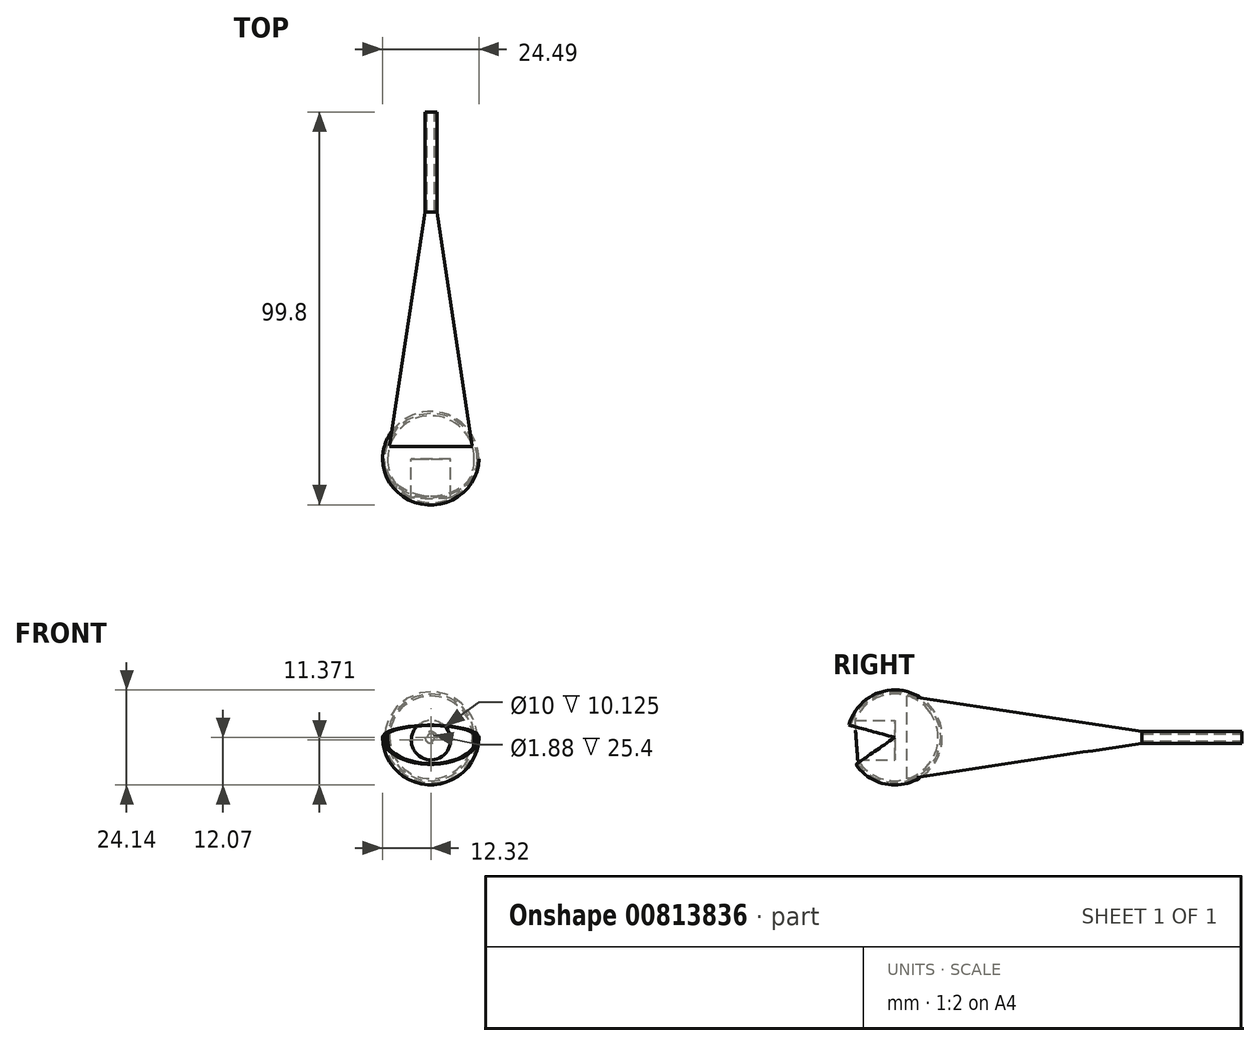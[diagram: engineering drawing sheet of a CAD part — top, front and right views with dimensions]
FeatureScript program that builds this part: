
annotation { "Feature Type Name" : "Feature", "Feature Type Description" : "" }
export const myFeature = defineFeature(function(context is Context, id is Id, definition is map)
    precondition{}
    {
        {
            var Q0;
            Q0=qCreatedBy(makeId("Front.planeOp"),FACE);
            var sketch = newSketch(context, id + "F0", { "sketchPlane" : qUnion([Q0])});
            skPoint(sketch, "E0.end.orphan", {"position": v(45.63, 0) * mm});
            skPoint(sketch, "E0.start.orphan", {"position": v(-38.44, 0) * mm});
            skArc(sketch, "E1", {"start": v(11, 0) * mm, "mid": v(0, 11) * mm, "end": v(-11, 0) * mm});
            skLineSegment(sketch, "E2", {"start": v(0, 0) * mm, "end": v(-11, 0) * mm});
            skLineSegment(sketch, "E3", {"start": v(-11, 0) * mm, "end": v(11, 0) * mm});
            skArc(sketch, "E4", {"start": v(11.75, 0) * mm, "mid": v(0, 11.59) * mm, "end": v(-11.74, 0) * mm});
            skArc(sketch, "E5", {"start": v(12.17, 0) * mm, "mid": v(-0.07, 12.07) * mm, "end": v(-12.32, 0) * mm});
            skLineSegment(sketch, "E6", {"start": v(-12.32, 0) * mm, "end": v(-11.74, 0) * mm});
            skLineSegment(sketch, "E7", {"start": v(11.75, 0) * mm, "end": v(12.17, 0) * mm});
            skSolve(sketch);
        }
        {
            var Q0;
            {var subQ0=sQuery(id+"F0.wireOp",EDGE,"E1");Q0=makeQuery(id+"F0.imprint","IMPRINT",FACE,{"disambiguationData":[TD([[makeQuery(id+"F0.imprint","IMPRINT",EDGE,{"derivedFrom":subQ0}),1.0]])]});}
            var Q1;
            Q1=sQuery(id+"F0.wireOp",EDGE,"E3");
            revolve(context, id + "F1", {"surfaceOperationType" : NewSurfaceOperationType.NEW, "entities" : qUnion([Q0]), "axis" : qUnion([Q1]), "revolveType" : RevolveType.FULL});
        }
        {
            var Q0;
            Q0=qCreatedBy(makeId("Front.planeOp"),FACE);
            var sketch = newSketch(context, id + "F2", { "sketchPlane" : qUnion([Q0])});
            skCircle(sketch, "E8", {"center": v(0, -0.7) * mm, "radius": 5 * mm});
            skSolve(sketch);
        }
        {
            var Q0;
            Q0 = qSketchRegion(id + "F2", true);
            extrude(context, id + "F3", {"entities" : qUnion([Q0]), "operationType" : NewBodyOperationType.REMOVE, "depth" : 11.43 * mm, "offsetDistance" : 25.4 * mm});
        }
        {
            var Q0;
            Q0=makeQuery(id+"F0.imprint","IMPRINT",FACE,{"disambiguationData":[TD([[makeQuery(id+"F0.imprint","IMPRINT",EDGE,{"derivedFrom":sQuery(id+"F0.wireOp",EDGE,"E4")}),-1.0]])]});
            var Q1;
            Q1=sQuery(id+"F0.wireOp",EDGE,"E3");
            revolve(context, id + "F4", {"surfaceOperationType" : NewSurfaceOperationType.NEW, "entities" : qUnion([Q0]), "axis" : qUnion([Q1]), "revolveType" : RevolveType.TWO_DIRECTIONS, "oppositeDirection" : true, "angle" : 235 * degree, "angleBack" : 285 * degree});
        }
        {
            var Q0;
            Q0=qCreatedBy(makeId("Front.planeOp"),FACE);
            cPlane(context, id + "F5", {"entities" : qUnion([Q0]), "cplaneType" : CPlaneType.OFFSET, "offset" : 3.12 * mm, "oppositeDirection" : true, "width" : 152.4 * mm, "height" : 152.4 * mm});
        }
        {
            var Q0;
            Q0=qCreatedBy(id+"F5.planeOp",FACE);
            var sketch = newSketch(context, id + "F6", { "sketchPlane" : qUnion([Q0])});
            skCircle(sketch, "E9", {"center": v(0, 0) * mm, "radius": 10.5 * mm});
            skSolve(sketch);
        }
        {
            var Q0;
            Q0=qCreatedBy(makeId("Front.planeOp"),FACE);
            cPlane(context, id + "F7", {"entities" : qUnion([Q0]), "cplaneType" : CPlaneType.OFFSET, "offset" : 62.74 * mm, "oppositeDirection" : true, "width" : 152.4 * mm, "height" : 152.4 * mm});
        }
        {
            var Q0;
            Q0=qCreatedBy(id+"F7.planeOp",FACE);
            var sketch = newSketch(context, id + "F8", { "sketchPlane" : qUnion([Q0])});
            skPoint(sketch, "E10.center.orphan", {"position": v(-1.46, 0) * mm});
            skCircle(sketch, "E11", {"center": v(0, 0) * mm, "radius": 1.5 * mm});
            skSolve(sketch);
        }
        {
            var Q0;
            Q0=makeQuery(id+"F6.imprint","IMPRINT",FACE,{"disambiguationData":[TD([[makeQuery(id+"F6.imprint","IMPRINT",EDGE,{"derivedFrom":sQuery(id+"F6.wireOp",EDGE,"E9")}),1.0]])]});
            var Q1;
            Q1=makeQuery(id+"F8.imprint","IMPRINT",FACE,{"disambiguationData":[TD([[makeQuery(id+"F8.imprint","IMPRINT",EDGE,{"derivedFrom":sQuery(id+"F8.wireOp",EDGE,"E11")}),1.0]])]});
            loft(context, id + "F9", {"sheetProfilesArray" : [{ "sheetProfileEntities" : qUnion([Q0]) }, { "sheetProfileEntities" : qUnion([Q1]) }]});
        }
        {
            var Q0;
            Q0=makeQuery(id+"F9.opLoft","CAP_FACE",FACE,{"disambiguationData":[OSD([makeQuery(id+"F8.imprint","IMPRINT",FACE,{"disambiguationData":[TD([[makeQuery(id+"F8.imprint","IMPRINT",EDGE,{"derivedFrom":sQuery(id+"F8.wireOp",EDGE,"E11")}),1.0]])]})])],"isStart":true});
            extrude(context, id + "F10", {"entities" : qUnion([Q0]), "operationType" : NewBodyOperationType.ADD, "depth" : 25.4 * mm, "offsetDistance" : 25.4 * mm});
        }
        {
            var Q0;
            Q0=makeQuery(id+"F10.opExtrude","CAP_FACE",FACE,{"disambiguationData":[OSD([makeQuery(id+"F8.imprint","IMPRINT",FACE,{"disambiguationData":[TD([[makeQuery(id+"F8.imprint","IMPRINT",EDGE,{"derivedFrom":sQuery(id+"F8.wireOp",EDGE,"E11")}),1.0]])]})])],"isStart":false});
            var sketch = newSketch(context, id + "F11", { "sketchPlane" : qUnion([Q0])});
            skCircle(sketch, "E12", {"center": v(0, 0) * mm, "radius": 0.94 * mm});
            skSolve(sketch);
        }
        {
            var Q0;
            Q0=makeQuery(id+"F11.imprint","IMPRINT",FACE,{"disambiguationData":[TD([[makeQuery(id+"F11.imprint","IMPRINT",EDGE,{"derivedFrom":sQuery(id+"F11.wireOp",EDGE,"E12")}),1.0]])]});
            extrude(context, id + "F12", {"entities" : qUnion([Q0]), "operationType" : NewBodyOperationType.REMOVE, "oppositeDirection" : true, "depth" : 25.4 * mm, "offsetDistance" : 25.4 * mm});
        }
    });
